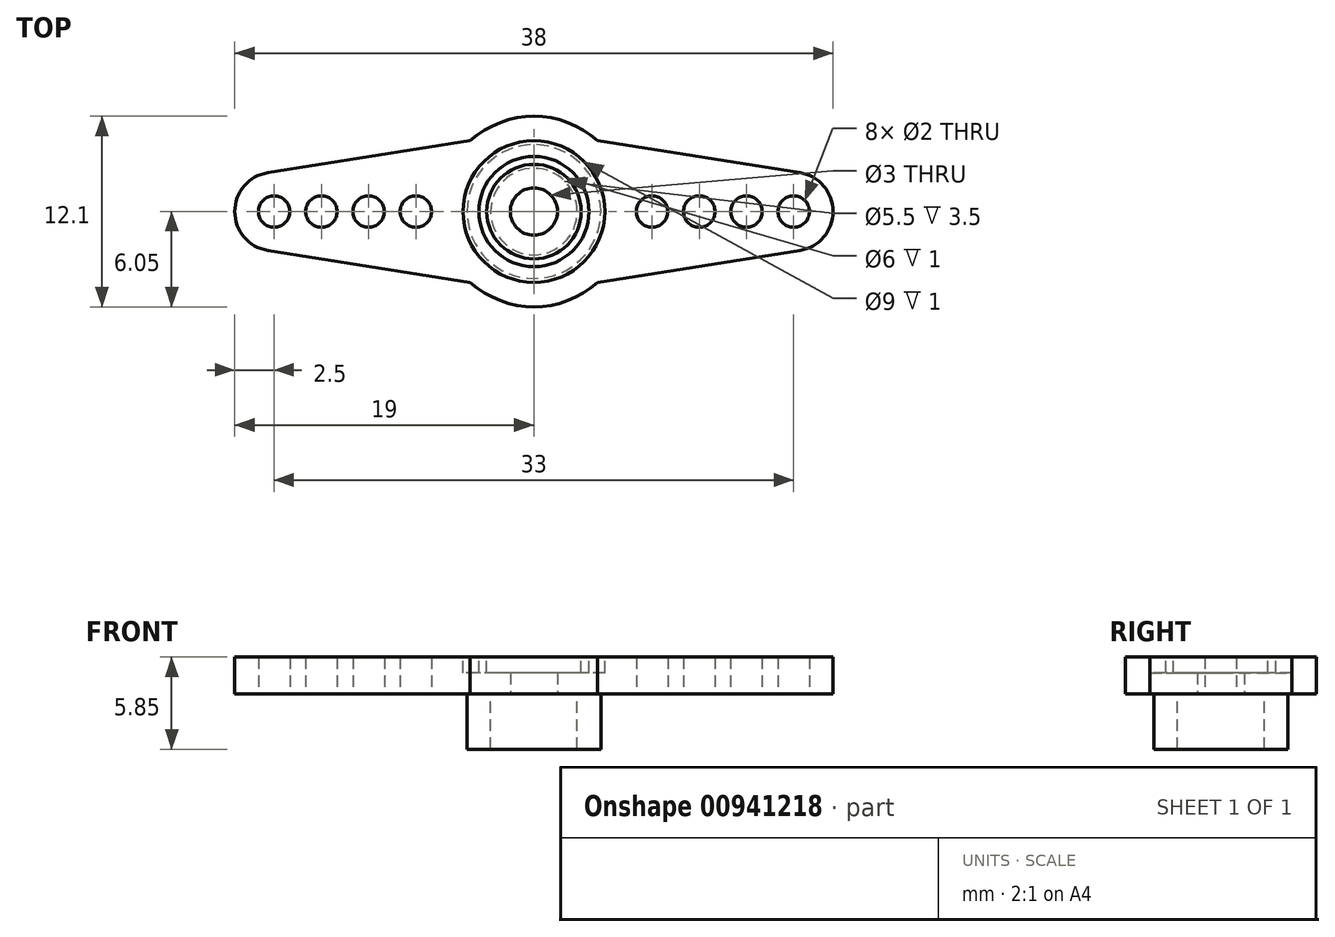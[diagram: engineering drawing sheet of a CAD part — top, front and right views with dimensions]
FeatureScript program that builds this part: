
annotation { "Feature Type Name" : "Feature", "Feature Type Description" : "" }
export const myFeature = defineFeature(function(context is Context, id is Id, definition is map)
    precondition{}
    {
        {
            var Q0;
            Q0=qCreatedBy(makeId("Top.planeOp"),FACE);
            var sketch = newSketch(context, id + "F0", { "sketchPlane" : qUnion([Q0])});
            skArc(sketch, "E0", {"start": v(-4.04, -4.5) * mm, "mid": v(0, -6.05) * mm, "end": v(4.04, -4.5) * mm});
            skArc(sketch, "E1", {"start": v(-16.9, 2.47) * mm, "mid": v(-19, 0) * mm, "end": v(-16.9, -2.47) * mm});
            skLineSegment(sketch, "E2", {"start": v(-16.9, 2.47) * mm, "end": v(-4.04, 4.5) * mm});
            skLineSegment(sketch, "E3.MirrorCS", {"start": v(-16.9, -2.47) * mm, "end": v(-4.04, -4.5) * mm});
            skLineSegment(sketch, "E4.MirrorCS", {"start": v(16.9, 2.47) * mm, "end": v(4.04, 4.5) * mm});
            skArc(sketch, "E5.MirrorC", {"start": v(16.9, 2.47) * mm, "mid": v(19, 0) * mm, "end": v(16.9, -2.47) * mm});
            skLineSegment(sketch, "E6.MirrorCS", {"start": v(16.9, -2.47) * mm, "end": v(4.04, -4.5) * mm});
            skArc(sketch, "E7.trimOffspring", {"start": v(4.04, 4.5) * mm, "mid": v(0, 6.05) * mm, "end": v(-4.04, 4.5) * mm});
            skSolve(sketch);
        }
        {
            var Q0;
            Q0 = qSketchRegion(id + "F0", true);
            extrude(context, id + "F1", {"entities" : qUnion([Q0]), "depth" : 2.35 * mm, "offsetDistance" : 25 * mm});
        }
        {
            var Q0;
            Q0=makeQuery(id+"F1.opExtrude","CAP_FACE",FACE,{"disambiguationData":[OSD([sQuery(id+"F0.wireOp",EDGE,"E0"),sQuery(id+"F0.wireOp",EDGE,"E1"),sQuery(id+"F0.wireOp",EDGE,"E2"),sQuery(id+"F0.wireOp",EDGE,"E3.MirrorCS"),sQuery(id+"F0.wireOp",EDGE,"E4.MirrorCS"),sQuery(id+"F0.wireOp",EDGE,"E5.MirrorC"),sQuery(id+"F0.wireOp",EDGE,"E6.MirrorCS"),sQuery(id+"F0.wireOp",EDGE,"E7.trimOffspring")])],"isStart":true});
            var sketch = newSketch(context, id + "F2", { "sketchPlane" : qUnion([Q0])});
            skCircle(sketch, "E8", {"center": v(0, 0) * mm, "radius": 2.75 * mm});
            skCircle(sketch, "E9", {"center": v(0, 0) * mm, "radius": 4.25 * mm});
            skSolve(sketch);
        }
        {
            var Q0;
            Q0 = qSketchRegion(id + "F2", true);
            extrude(context, id + "F3", {"entities" : qUnion([Q0]), "operationType" : NewBodyOperationType.ADD, "depth" : 3.5 * mm, "offsetDistance" : 25 * mm});
        }
        {
            var Q0;
            {var subQ0=sQuery(id+"F0.wireOp",EDGE,"E2");var subQ1=sQuery(id+"F0.wireOp",EDGE,"E1");var subQ2=sQuery(id+"F0.wireOp",EDGE,"E3.MirrorCS");var subQ3=sQuery(id+"F0.wireOp",EDGE,"E0");var subQ4=sQuery(id+"F0.wireOp",EDGE,"E4.MirrorCS");var subQ5=sQuery(id+"F0.wireOp",EDGE,"E5.MirrorC");var subQ6=sQuery(id+"F0.wireOp",EDGE,"E6.MirrorCS");var subQ7=sQuery(id+"F0.wireOp",EDGE,"E7.trimOffspring");Q0=makeQuery(id+"F3.boolean.opBoolean","SPLIT",FACE,{"disambiguationData":[TD([makeQuery(id+"F1.opExtrude","SWEPT_FACE",FACE,{"disambiguationData":[OSD([subQ3])]})])],"derivedFrom":makeQuery(id+"F1.opExtrude","CAP_FACE",FACE,{"disambiguationData":[OSD([subQ3,subQ1,subQ0,subQ2,subQ4,subQ5,subQ6,subQ7])],"isStart":true})});}
            var sketch = newSketch(context, id + "F4", { "sketchPlane" : qUnion([Q0])});
            skCircle(sketch, "E10", {"center": v(0, 0) * mm, "radius": 1.5 * mm});
            skCircle(sketch, "E11", {"center": v(-7.5, 0) * mm, "radius": 1 * mm});
            skCircle(sketch, "E12", {"center": v(-10.5, 0) * mm, "radius": 1 * mm});
            skCircle(sketch, "E13", {"center": v(-13.5, 0) * mm, "radius": 1 * mm});
            skCircle(sketch, "E14", {"center": v(-16.5, 0) * mm, "radius": 1 * mm});
            skCircle(sketch, "E15.MirrorC", {"center": v(7.5, 0) * mm, "radius": 1 * mm});
            skCircle(sketch, "E16.MirrorC", {"center": v(10.5, 0) * mm, "radius": 1 * mm});
            skCircle(sketch, "E17.MirrorC", {"center": v(13.5, 0) * mm, "radius": 1 * mm});
            skCircle(sketch, "E18.MirrorC", {"center": v(16.5, 0) * mm, "radius": 1 * mm});
            skSolve(sketch);
        }
        {
            var Q0;
            Q0 = qSketchRegion(id + "F4", true);
            extrude(context, id + "F5", {"entities" : qUnion([Q0]), "operationType" : NewBodyOperationType.REMOVE, "oppositeDirection" : true, "depth" : 25 * mm, "offsetDistance" : 25 * mm});
        }
        {
            var Q0;
            Q0=makeQuery(id+"F1.opExtrude","CAP_FACE",FACE,{"disambiguationData":[OSD([sQuery(id+"F0.wireOp",EDGE,"E0"),sQuery(id+"F0.wireOp",EDGE,"E1"),sQuery(id+"F0.wireOp",EDGE,"E2"),sQuery(id+"F0.wireOp",EDGE,"E3.MirrorCS"),sQuery(id+"F0.wireOp",EDGE,"E4.MirrorCS"),sQuery(id+"F0.wireOp",EDGE,"E5.MirrorC"),sQuery(id+"F0.wireOp",EDGE,"E6.MirrorCS"),sQuery(id+"F0.wireOp",EDGE,"E7.trimOffspring")])],"isStart":false});
            var sketch = newSketch(context, id + "F6", { "sketchPlane" : qUnion([Q0])});
            skCircle(sketch, "E19", {"center": v(0, 0) * mm, "radius": 3 * mm});
            skCircle(sketch, "E20", {"center": v(0, 0) * mm, "radius": 3.5 * mm});
            skCircle(sketch, "E21", {"center": v(0, 0) * mm, "radius": 4.5 * mm});
            skCircle(sketch, "E22.0", {"center": v(0, 0) * mm, "radius": 1.5 * mm});
            skSolve(sketch);
        }
        {
            var Q0;
            Q0 = qSketchRegion(id + "F6", true);
            var Q1;
            Q1=makeQuery(id+"F6.imprint","IMPRINT",FACE,{"disambiguationData":[TD([[makeQuery(id+"F6.imprint","IMPRINT",EDGE,{"derivedFrom":sQuery(id+"F6.wireOp",EDGE,"E19")}),1.0]])]});
            extrude(context, id + "F7", {"entities" : qUnion([Q0, Q1]), "operationType" : NewBodyOperationType.REMOVE, "oppositeDirection" : true, "depth" : 1 * mm, "offsetDistance" : 25 * mm});
        }
    });
